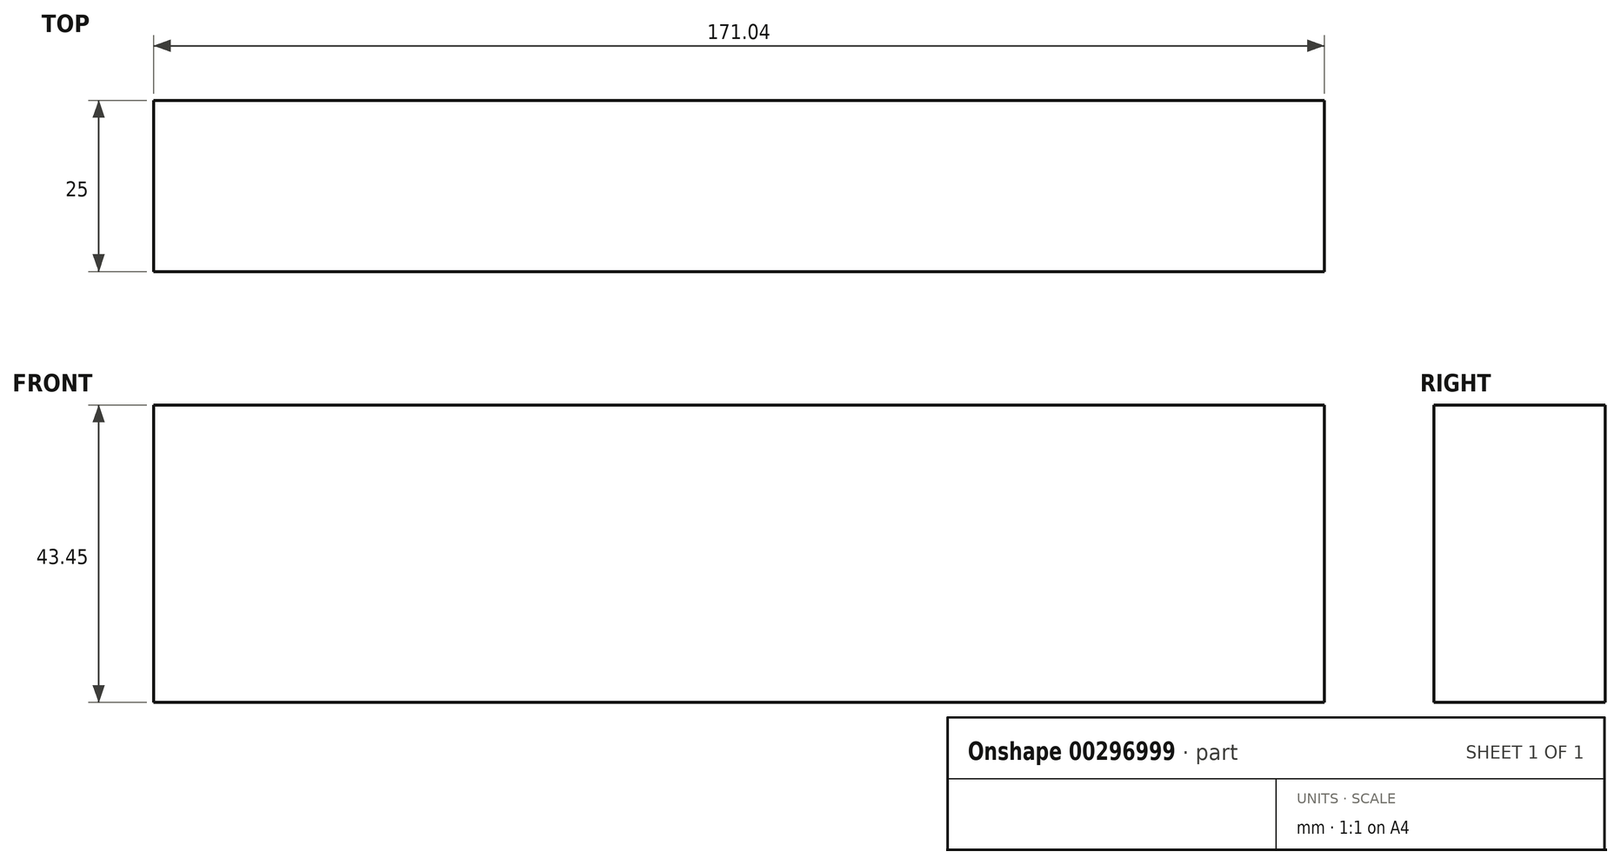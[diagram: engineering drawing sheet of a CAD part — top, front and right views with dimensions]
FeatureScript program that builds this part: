
annotation { "Feature Type Name" : "Feature", "Feature Type Description" : "" }
export const myFeature = defineFeature(function(context is Context, id is Id, definition is map)
    precondition{}
    {
        {
            var Q0;
            Q0=qCreatedBy(makeId("Front.planeOp"),FACE);
            var sketch = newSketch(context, id + "F0", { "sketchPlane" : qUnion([Q0])});
            skLineSegment(sketch, "E0.bottom", {"start": v(-48.68, 59.62) * mm, "end": v(122.36, 59.62) * mm});
            skLineSegment(sketch, "E0.top", {"start": v(-48.68, 16.17) * mm, "end": v(122.36, 16.17) * mm});
            skLineSegment(sketch, "E0.left", {"start": v(-48.68, 59.62) * mm, "end": v(-48.68, 16.17) * mm});
            skLineSegment(sketch, "E0.right", {"start": v(122.36, 59.62) * mm, "end": v(122.36, 16.17) * mm});
            skSolve(sketch);
        }
        {
            var Q0;
            Q0 = qSketchRegion(id + "F0", true);
            extrude(context, id + "F1", {"entities" : qUnion([Q0]), "depth" : 25 * mm});
        }
    });
